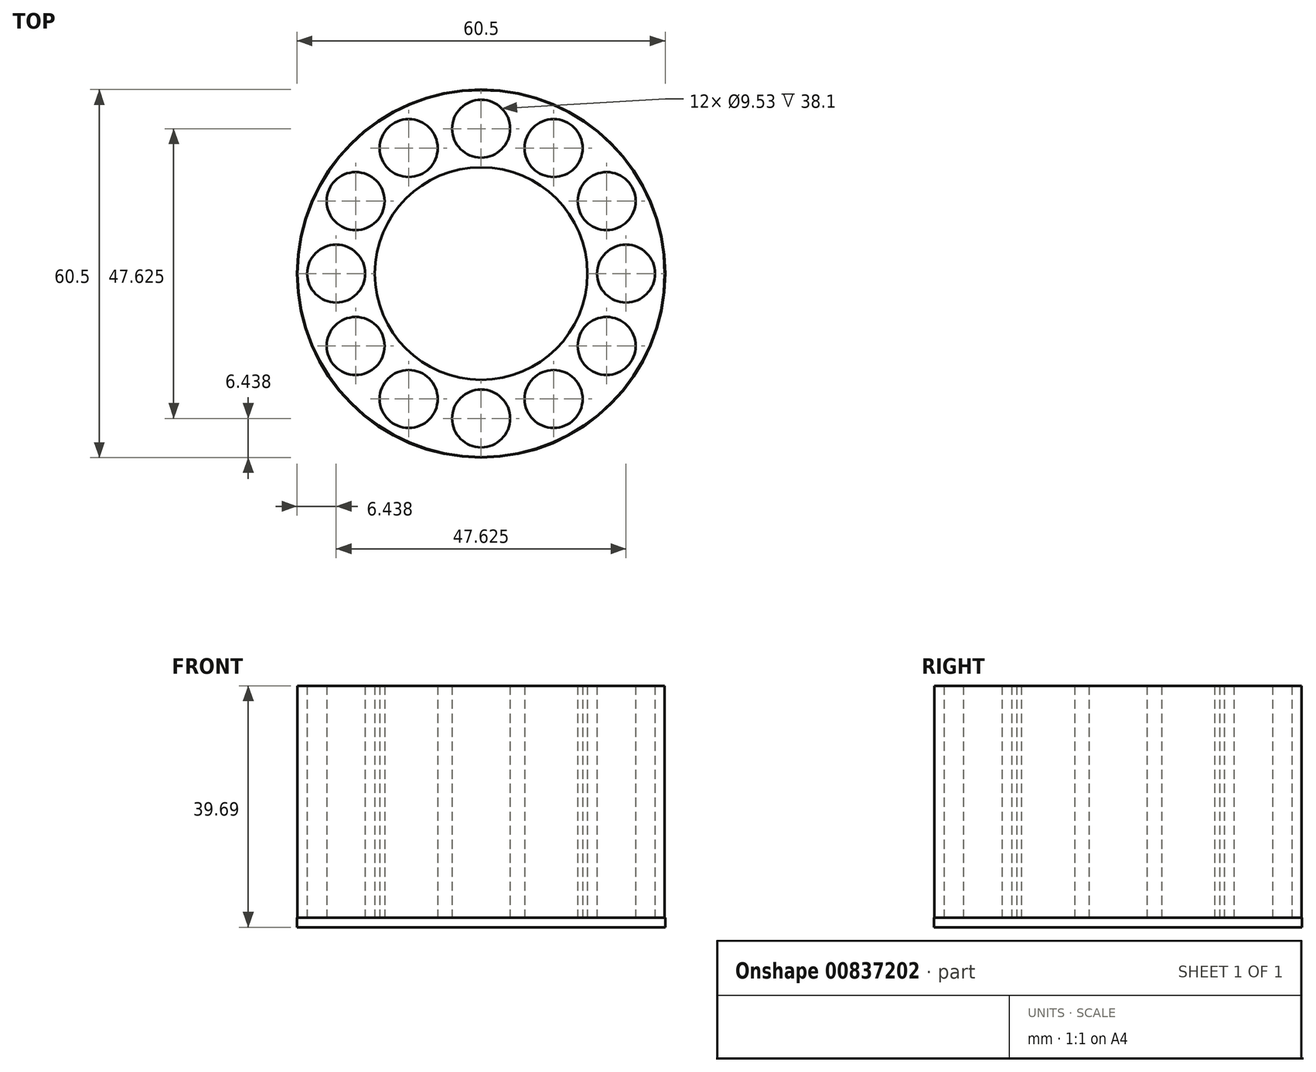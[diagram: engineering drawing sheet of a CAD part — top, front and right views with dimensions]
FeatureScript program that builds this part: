
annotation { "Feature Type Name" : "Feature", "Feature Type Description" : "" }
export const myFeature = defineFeature(function(context is Context, id is Id, definition is map)
    precondition{}
    {
        {
            var Q0;
            Q0=qCreatedBy(makeId("Top.planeOp"),FACE);
            var sketch = newSketch(context, id + "F0", { "sketchPlane" : qUnion([Q0])});
            skCircle(sketch, "E0", {"center": v(0, 23.81) * mm, "radius": 4.76 * mm});
            skCircle(sketch, "E1.1.0", {"center": v(11.9, 20.62) * mm, "radius": 4.76 * mm});
            skCircle(sketch, "E1.2.0", {"center": v(20.62, 11.9) * mm, "radius": 4.76 * mm});
            skCircle(sketch, "E1.3.0", {"center": v(23.81, 0) * mm, "radius": 4.76 * mm});
            skCircle(sketch, "E1.4.0", {"center": v(20.62, -11.9) * mm, "radius": 4.76 * mm});
            skCircle(sketch, "E1.5.0", {"center": v(11.9, -20.62) * mm, "radius": 4.76 * mm});
            skCircle(sketch, "E1.6.0", {"center": v(0, -23.81) * mm, "radius": 4.76 * mm});
            skCircle(sketch, "E1.7.0", {"center": v(-11.9, -20.62) * mm, "radius": 4.76 * mm});
            skCircle(sketch, "E1.8.0", {"center": v(-20.62, -11.9) * mm, "radius": 4.76 * mm});
            skCircle(sketch, "E1.9.0", {"center": v(-23.81, 0) * mm, "radius": 4.76 * mm});
            skCircle(sketch, "E1.10.0", {"center": v(-20.62, 11.9) * mm, "radius": 4.76 * mm});
            skCircle(sketch, "E1.11.0", {"center": v(-11.9, 20.62) * mm, "radius": 4.76 * mm});
            skPoint(sketch, "E1.center", {"position": v(0, 0) * mm});
            skLineSegment(sketch, "E1.anchor1", {"start": v(0, 0) * mm, "end": v(0, 23.81) * mm, "construction": true});
            skLineSegment(sketch, "E1.anchor2", {"start": v(0, 0) * mm, "end": v(-11.9, 20.62) * mm, "construction": true});
            skCircle(sketch, "E2", {"center": v(0, 0) * mm, "radius": 17.46 * mm});
            skCircle(sketch, "E3", {"center": v(0, 0) * mm, "radius": 30.16 * mm});
            skSolve(sketch);
        }
        {
            var Q0;
            {var subQ0=sQuery(id+"F0.wireOp",EDGE,"zM0cmyA9-pMgm-0OsQ-U8Jh-3t3VWyZ2nu6r");var subQ1=sQuery(id+"F0.wireOp",EDGE,"E1.9.0");var subQ2=makeQuery(id+"F0.imprint","INTERSECT",VERTEX,{"derivedFrom":[subQ1,subQ0]});Q0=makeQuery(id+"F0.imprint","IMPRINT",FACE,{"disambiguationData":[TD([[makeQuery(id+"F0.imprint","IMPRINT",EDGE,{"disambiguationData":[TD([[subQ2,1.0]])],"derivedFrom":subQ1}),-1.0]])]});}
            var Q1;
            {var subQ0=sQuery(id+"F0.wireOp",EDGE,"zM0cmyA9-pMgm-0OsQ-U8Jh-3t3VWyZ2nu6r");var subQ1=sQuery(id+"F0.wireOp",EDGE,"E1.10.0");var subQ2=makeQuery(id+"F0.imprint","INTERSECT",VERTEX,{"derivedFrom":[subQ1,subQ0]});Q1=makeQuery(id+"F0.imprint","IMPRINT",FACE,{"disambiguationData":[TD([[makeQuery(id+"F0.imprint","IMPRINT",EDGE,{"disambiguationData":[TD([[subQ2,1.0]])],"derivedFrom":subQ1}),-1.0]])]});}
            var Q2;
            {var subQ0=sQuery(id+"F0.wireOp",EDGE,"zM0cmyA9-pMgm-0OsQ-U8Jh-3t3VWyZ2nu6r");var subQ1=sQuery(id+"F0.wireOp",EDGE,"E0");var subQ2=makeQuery(id+"F0.imprint","INTERSECT",VERTEX,{"derivedFrom":[subQ1,subQ0]});Q2=makeQuery(id+"F0.imprint","IMPRINT",FACE,{"disambiguationData":[TD([[makeQuery(id+"F0.imprint","IMPRINT",EDGE,{"disambiguationData":[TD([[subQ2,-1.0]])],"derivedFrom":subQ1}),-1.0]])]});}
            var Q3;
            {var subQ0=sQuery(id+"F0.wireOp",EDGE,"zM0cmyA9-pMgm-0OsQ-U8Jh-3t3VWyZ2nu6r");var subQ1=sQuery(id+"F0.wireOp",EDGE,"E0");var subQ2=makeQuery(id+"F0.imprint","INTERSECT",VERTEX,{"derivedFrom":[subQ1,subQ0]});Q3=makeQuery(id+"F0.imprint","IMPRINT",FACE,{"disambiguationData":[TD([[makeQuery(id+"F0.imprint","IMPRINT",EDGE,{"disambiguationData":[TD([[subQ2,1.0]])],"derivedFrom":subQ1}),-1.0]])]});}
            var Q4;
            {var subQ0=sQuery(id+"F0.wireOp",EDGE,"zM0cmyA9-pMgm-0OsQ-U8Jh-3t3VWyZ2nu6r");var subQ1=sQuery(id+"F0.wireOp",EDGE,"E1.1.0");var subQ2=makeQuery(id+"F0.imprint","INTERSECT",VERTEX,{"derivedFrom":[subQ1,subQ0]});Q4=makeQuery(id+"F0.imprint","IMPRINT",FACE,{"disambiguationData":[TD([[makeQuery(id+"F0.imprint","IMPRINT",EDGE,{"disambiguationData":[TD([[subQ2,1.0]])],"derivedFrom":subQ1}),-1.0]])]});}
            var Q5;
            {var subQ0=sQuery(id+"F0.wireOp",EDGE,"zM0cmyA9-pMgm-0OsQ-U8Jh-3t3VWyZ2nu6r");var subQ1=sQuery(id+"F0.wireOp",EDGE,"E1.2.0");var subQ2=makeQuery(id+"F0.imprint","INTERSECT",VERTEX,{"derivedFrom":[subQ1,subQ0]});Q5=makeQuery(id+"F0.imprint","IMPRINT",FACE,{"disambiguationData":[TD([[makeQuery(id+"F0.imprint","IMPRINT",EDGE,{"disambiguationData":[TD([[subQ2,1.0]])],"derivedFrom":subQ1}),-1.0]])]});}
            var Q6;
            {var subQ0=sQuery(id+"F0.wireOp",EDGE,"zM0cmyA9-pMgm-0OsQ-U8Jh-3t3VWyZ2nu6r");var subQ1=sQuery(id+"F0.wireOp",EDGE,"E1.3.0");var subQ2=makeQuery(id+"F0.imprint","INTERSECT",VERTEX,{"derivedFrom":[subQ1,subQ0]});Q6=makeQuery(id+"F0.imprint","IMPRINT",FACE,{"disambiguationData":[TD([[makeQuery(id+"F0.imprint","IMPRINT",EDGE,{"disambiguationData":[TD([[subQ2,1.0]])],"derivedFrom":subQ1}),-1.0]])]});}
            var Q7;
            {var subQ0=sQuery(id+"F0.wireOp",EDGE,"zM0cmyA9-pMgm-0OsQ-U8Jh-3t3VWyZ2nu6r");var subQ1=sQuery(id+"F0.wireOp",EDGE,"E1.4.0");var subQ2=makeQuery(id+"F0.imprint","INTERSECT",VERTEX,{"derivedFrom":[subQ1,subQ0]});Q7=makeQuery(id+"F0.imprint","IMPRINT",FACE,{"disambiguationData":[TD([[makeQuery(id+"F0.imprint","IMPRINT",EDGE,{"disambiguationData":[TD([[subQ2,1.0]])],"derivedFrom":subQ1}),-1.0]])]});}
            var Q8;
            {var subQ0=sQuery(id+"F0.wireOp",EDGE,"zM0cmyA9-pMgm-0OsQ-U8Jh-3t3VWyZ2nu6r");var subQ1=sQuery(id+"F0.wireOp",EDGE,"E1.5.0");var subQ2=makeQuery(id+"F0.imprint","INTERSECT",VERTEX,{"derivedFrom":[subQ1,subQ0]});Q8=makeQuery(id+"F0.imprint","IMPRINT",FACE,{"disambiguationData":[TD([[makeQuery(id+"F0.imprint","IMPRINT",EDGE,{"disambiguationData":[TD([[subQ2,1.0]])],"derivedFrom":subQ1}),-1.0]])]});}
            var Q9;
            {var subQ0=sQuery(id+"F0.wireOp",EDGE,"zM0cmyA9-pMgm-0OsQ-U8Jh-3t3VWyZ2nu6r");var subQ1=sQuery(id+"F0.wireOp",EDGE,"E1.6.0");var subQ2=makeQuery(id+"F0.imprint","INTERSECT",VERTEX,{"derivedFrom":[subQ1,subQ0]});Q9=makeQuery(id+"F0.imprint","IMPRINT",FACE,{"disambiguationData":[TD([[makeQuery(id+"F0.imprint","IMPRINT",EDGE,{"disambiguationData":[TD([[subQ2,1.0]])],"derivedFrom":subQ1}),-1.0]])]});}
            var Q10;
            {var subQ0=sQuery(id+"F0.wireOp",EDGE,"zM0cmyA9-pMgm-0OsQ-U8Jh-3t3VWyZ2nu6r");var subQ1=sQuery(id+"F0.wireOp",EDGE,"E1.7.0");var subQ2=makeQuery(id+"F0.imprint","INTERSECT",VERTEX,{"derivedFrom":[subQ1,subQ0]});Q10=makeQuery(id+"F0.imprint","IMPRINT",FACE,{"disambiguationData":[TD([[makeQuery(id+"F0.imprint","IMPRINT",EDGE,{"disambiguationData":[TD([[subQ2,1.0]])],"derivedFrom":subQ1}),-1.0]])]});}
            var Q11;
            {var subQ0=sQuery(id+"F0.wireOp",EDGE,"zM0cmyA9-pMgm-0OsQ-U8Jh-3t3VWyZ2nu6r");var subQ1=sQuery(id+"F0.wireOp",EDGE,"E1.8.0");var subQ2=makeQuery(id+"F0.imprint","INTERSECT",VERTEX,{"derivedFrom":[subQ1,subQ0]});Q11=makeQuery(id+"F0.imprint","IMPRINT",FACE,{"disambiguationData":[TD([[makeQuery(id+"F0.imprint","IMPRINT",EDGE,{"disambiguationData":[TD([[subQ2,1.0]])],"derivedFrom":subQ1}),-1.0]])]});}
            extrude(context, id + "F1", {"entities" : qUnion([Q0, Q1, Q2, Q3, Q4, Q5, Q6, Q7, Q8, Q9, Q10, Q11]), "depth" : 38.1 * mm, "offsetDistance" : 25.4 * mm});
        }
        {
            var Q0;
            Q0=makeQuery(id+"F1.opExtrude","CAP_FACE",FACE,{"disambiguationData":[OSD([sQuery(id+"F0.wireOp",EDGE,"E0"),sQuery(id+"F0.wireOp",EDGE,"E1.1.0"),sQuery(id+"F0.wireOp",EDGE,"E1.2.0"),sQuery(id+"F0.wireOp",EDGE,"E1.3.0"),sQuery(id+"F0.wireOp",EDGE,"E1.4.0"),sQuery(id+"F0.wireOp",EDGE,"E1.5.0"),sQuery(id+"F0.wireOp",EDGE,"E1.6.0"),sQuery(id+"F0.wireOp",EDGE,"E1.7.0"),sQuery(id+"F0.wireOp",EDGE,"E1.8.0"),sQuery(id+"F0.wireOp",EDGE,"E1.9.0"),sQuery(id+"F0.wireOp",EDGE,"E1.10.0"),sQuery(id+"F0.wireOp",EDGE,"E1.11.0"),sQuery(id+"F0.wireOp",EDGE,"E2"),sQuery(id+"F0.wireOp",EDGE,"E3")])],"isStart":true});
            var sketch = newSketch(context, id + "F2", { "sketchPlane" : qUnion([Q0])});
            skCircle(sketch, "E4", {"center": v(0, 0) * mm, "radius": 30.25 * mm});
            skSolve(sketch);
        }
        {
            var Q0;
            Q0 = qSketchRegion(id + "F2", true);
            extrude(context, id + "F3", {"entities" : qUnion([Q0]), "operationType" : NewBodyOperationType.ADD, "depth" : 1.59 * mm, "offsetDistance" : 25.4 * mm});
        }
    });
